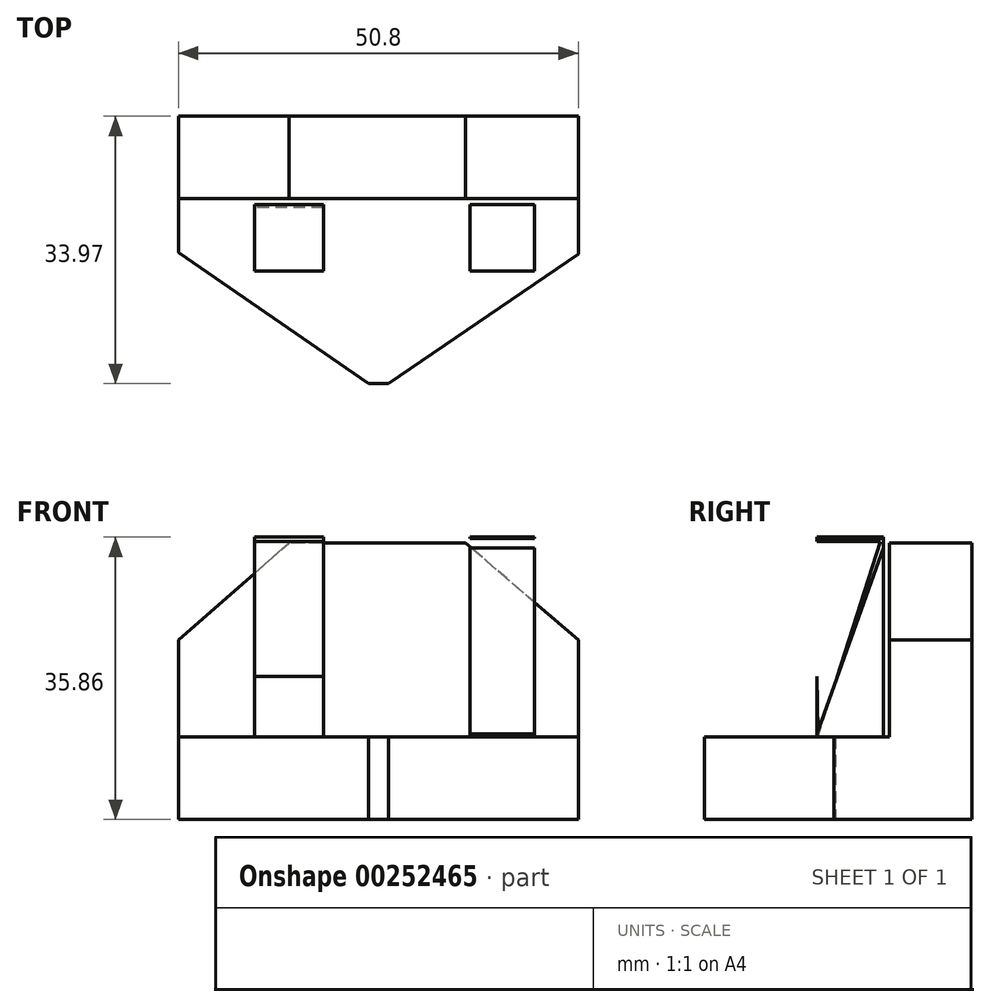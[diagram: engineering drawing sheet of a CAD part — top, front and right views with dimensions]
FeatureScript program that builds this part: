
annotation { "Feature Type Name" : "Feature", "Feature Type Description" : "" }
export const myFeature = defineFeature(function(context is Context, id is Id, definition is map)
    precondition{}
    {
        {
            var Q0;
            Q0=qCreatedBy(makeId("Right.planeOp"),FACE);
            var sketch = newSketch(context, id + "F0", { "sketchPlane" : qUnion([Q0])});
            skLineSegment(sketch, "E0", {"start": v(-33.97, 0) * mm, "end": v(-33.97, -10.46) * mm});
            skLineSegment(sketch, "E1", {"start": v(-33.97, 0) * mm, "end": v(-10.46, 0) * mm});
            skLineSegment(sketch, "E2", {"start": v(-10.46, 0) * mm, "end": v(-10.46, 24.63) * mm});
            skLineSegment(sketch, "E3", {"start": v(-10.46, 24.63) * mm, "end": v(0, 24.63) * mm});
            skLineSegment(sketch, "E4", {"start": v(0, -10.46) * mm, "end": v(-33.97, -10.46) * mm});
            skLineSegment(sketch, "E5", {"start": v(0, -10.46) * mm, "end": v(0, 24.63) * mm});
            skSolve(sketch);
        }
        {
            var Q0;
            Q0 = qSketchRegion(id + "F0", true);
            extrude(context, id + "F1", {"entities" : qUnion([Q0]), "depth" : 25.4 * mm, "hasSecondDirection" : true, "secondDirectionOppositeDirection" : true, "secondDirectionDepth" : 25.4 * mm});
        }
        {
            var Q0;
            Q0=qCreatedBy(makeId("Top.planeOp"),FACE);
            var sketch = newSketch(context, id + "F2", { "sketchPlane" : qUnion([Q0])});
            skLineSegment(sketch, "E6", {"start": v(-27.24, -16.04) * mm, "end": v(0, -34.83) * mm});
            skLineSegment(sketch, "E7", {"start": v(25.65, -17.34) * mm, "end": v(0, -34.83) * mm});
            skLineSegment(sketch, "E8", {"start": v(-27.24, -34.83) * mm, "end": v(0, -34.83) * mm});
            skLineSegment(sketch, "E9", {"start": v(-27.24, -34.83) * mm, "end": v(-27.24, -16.04) * mm});
            skLineSegment(sketch, "E10", {"start": v(25.65, -34.83) * mm, "end": v(0, -34.83) * mm});
            skLineSegment(sketch, "E11", {"start": v(25.65, -17.34) * mm, "end": v(25.65, -34.83) * mm});
            skSolve(sketch);
        }
        {
            var Q0;
            Q0 = qSketchRegion(id + "F2", true);
            extrude(context, id + "F3", {"entities" : qUnion([Q0]), "operationType" : NewBodyOperationType.REMOVE, "oppositeDirection" : true, "depth" : 25.4 * mm});
        }
        {
            var Q0;
            Q0=makeQuery(id+"F1.opExtrude","SWEPT_FACE",FACE,{"disambiguationData":[OSD([sQuery(id+"F0.wireOp",EDGE,"E2")])]});
            var sketch = newSketch(context, id + "F4", { "sketchPlane" : qUnion([Q0])});
            skLineSegment(sketch, "E12", {"start": v(-25.4, 12.31) * mm, "end": v(-11.37, 24.63) * mm});
            skLineSegment(sketch, "E13", {"start": v(-25.4, 12.31) * mm, "end": v(25.4, 12.31) * mm});
            skLineSegment(sketch, "E14", {"start": v(25.4, 12.31) * mm, "end": v(11.08, 24.63) * mm});
            skSolve(sketch);
        }
        {
            var Q0;
            {var subQ0=sQuery(id+"F4.wireOp",EDGE,"E12");Q0=makeQuery(id+"F4.imprint","IMPRINT",FACE,{"disambiguationData":[TD([[makeQuery(id+"F4.imprint","IMPRINT",EDGE,{"derivedFrom":subQ0}),1.0]])]});}
            var Q1;
            {var subQ0=sQuery(id+"F4.wireOp",EDGE,"E14");Q1=makeQuery(id+"F4.imprint","IMPRINT",FACE,{"disambiguationData":[TD([[makeQuery(id+"F4.imprint","IMPRINT",EDGE,{"derivedFrom":subQ0}),-1.0]])]});}
            extrude(context, id + "F5", {"entities" : qUnion([Q0, Q1]), "operationType" : NewBodyOperationType.REMOVE, "oppositeDirection" : true, "depth" : 25.4 * mm});
        }
        {
            var Q0;
            Q0=qCreatedBy(makeId("Top.planeOp"),FACE);
            var sketch = newSketch(context, id + "F6", { "sketchPlane" : qUnion([Q0])});
            skLineSegment(sketch, "E15", {"start": v(-15.74, -11.22) * mm, "end": v(-15.74, -19.68) * mm});
            skLineSegment(sketch, "E16", {"start": v(-15.74, -11.22) * mm, "end": v(-7, -11.22) * mm});
            skLineSegment(sketch, "E17", {"start": v(-7, -11.22) * mm, "end": v(-7, -19.68) * mm});
            skLineSegment(sketch, "E18", {"start": v(-7, -19.68) * mm, "end": v(-15.74, -19.68) * mm});
            skLineSegment(sketch, "E19", {"start": v(19.82, -11.22) * mm, "end": v(19.82, -19.68) * mm});
            skPoint(sketch, "E19.endSnap0", {"position": v(-11.37, -19.68) * mm});
            skLineSegment(sketch, "E20", {"start": v(19.82, -19.68) * mm, "end": v(11.66, -19.68) * mm});
            skLineSegment(sketch, "E21", {"start": v(11.66, -19.68) * mm, "end": v(11.66, -11.22) * mm});
            skLineSegment(sketch, "E22", {"start": v(11.66, -11.22) * mm, "end": v(19.82, -11.22) * mm});
            skSolve(sketch);
        }
        {
            var Q0;
            Q0 = qSketchRegion(id + "F6", true);
            extrude(context, id + "F7", {"entities" : qUnion([Q0]), "depth" : 25.4 * mm});
        }
        {
            var Q0;
            Q0=makeQuery(id+"F7.opExtrude","SWEPT_FACE",FACE,{"disambiguationData":[OSD([sQuery(id+"F6.wireOp",EDGE,"E19")])]});
            var sketch = newSketch(context, id + "F8", { "sketchPlane" : qUnion([Q0])});
            skLineSegment(sketch, "E23", {"start": v(-19.82, 0) * mm, "end": v(-19.82, 25.21) * mm});
            skLineSegment(sketch, "E24", {"start": v(-19.82, 25.21) * mm, "end": v(-10.78, 25.21) * mm});
            skLineSegment(sketch, "E25", {"start": v(-10.78, 25.21) * mm, "end": v(-19.82, 0) * mm});
            skSolve(sketch);
        }
        {
            var Q0;
            Q0 = qSketchRegion(id + "F8", true);
            extrude(context, id + "F9", {"entities" : qUnion([Q0]), "operationType" : NewBodyOperationType.REMOVE, "oppositeDirection" : true, "depth" : 25.4 * mm});
        }
        {
            var Q0;
            Q0=makeQuery(id+"F7.opExtrude","SWEPT_FACE",FACE,{"disambiguationData":[OSD([sQuery(id+"F6.wireOp",EDGE,"E15")])]});
            var sketch = newSketch(context, id + "F10", { "sketchPlane" : qUnion([Q0])});
            skLineSegment(sketch, "E26", {"start": v(20.03, 24.84) * mm, "end": v(11.6, 24.84) * mm});
            skLineSegment(sketch, "E27", {"start": v(11.6, 24.84) * mm, "end": v(19.52, 0) * mm});
            skLineSegment(sketch, "E28", {"start": v(19.52, 0) * mm, "end": v(20.03, 24.84) * mm});
            skSolve(sketch);
        }
        {
            var Q0;
            {var subQ0=sQuery(id+"F10.wireOp",EDGE,"E27");Q0=makeQuery(id+"F10.imprint","IMPRINT",FACE,{"disambiguationData":[TD([[makeQuery(id+"F10.imprint","IMPRINT",EDGE,{"derivedFrom":subQ0}),1.0]])]});}
            var Q1;
            Q1=sQuery(id+"F10.wireOp",EDGE,"E27");
            extrude(context, id + "F11", {"entities" : qUnion([Q0]), "operationType" : NewBodyOperationType.REMOVE, "surfaceEntities" : qUnion([Q1]), "oppositeDirection" : true, "depth" : 25.4 * mm});
        }
    });
